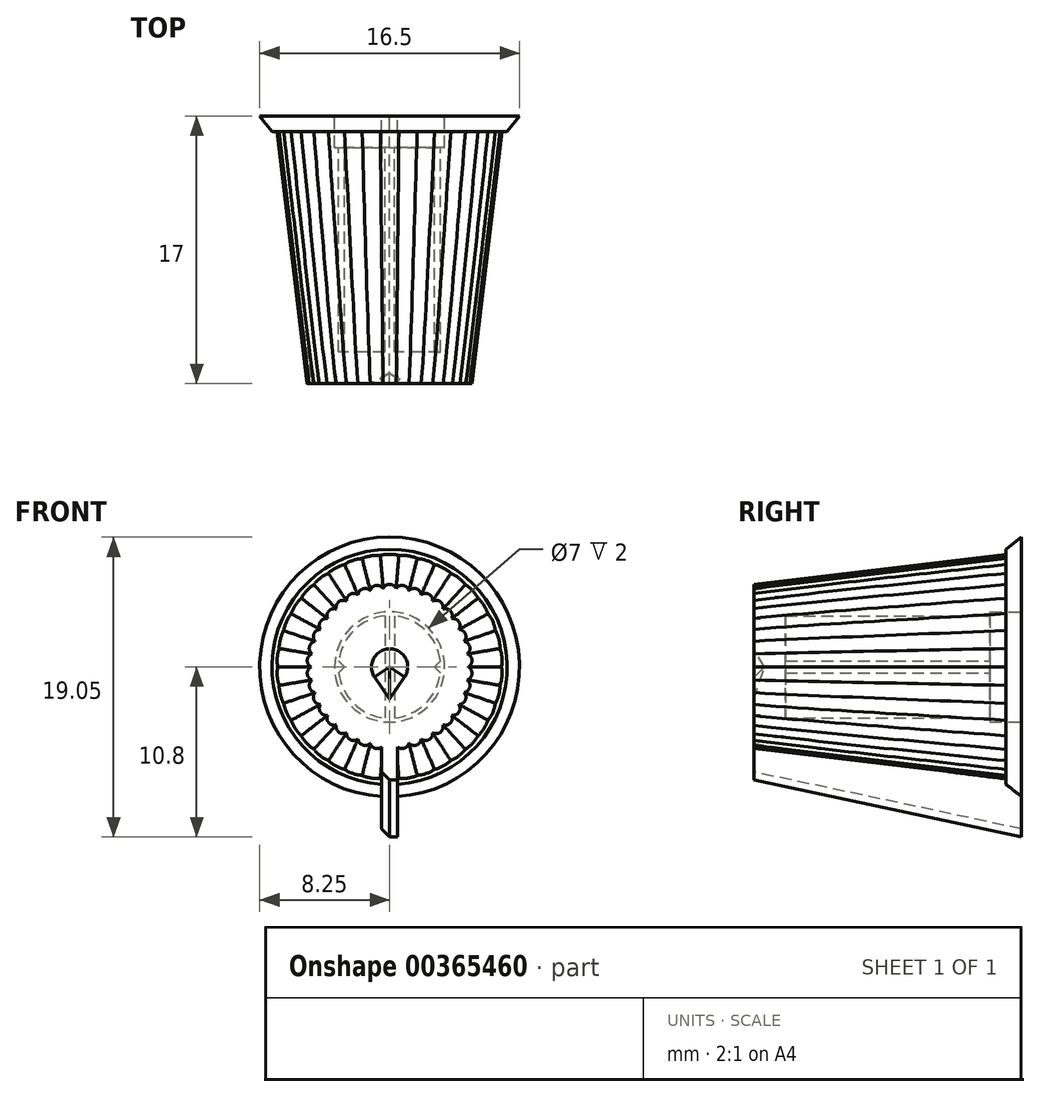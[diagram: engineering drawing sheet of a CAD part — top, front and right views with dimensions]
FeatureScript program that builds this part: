
annotation { "Feature Type Name" : "Feature", "Feature Type Description" : "" }
export const myFeature = defineFeature(function(context is Context, id is Id, definition is map)
    precondition{}
    {
        {
            var Q0;
            Q0=qCreatedBy(makeId("Front.planeOp"),FACE);
            var sketch = newSketch(context, id + "F0", { "sketchPlane" : qUnion([Q0])});
            skCircle(sketch, "E0", {"center": v(0, 0) * mm, "radius": 8.25 * mm});
            skSolve(sketch);
        }
        {
            var Q0;
            Q0 = qSketchRegion(id + "F0", true);
            extrude(context, id + "F1", {"entities" : qUnion([Q0]), "depth" : 1 * mm, "hasDraft" : true, "draftAngle" : 38 * degree, "draftPullDirection" : true});
        }
        {
            var Q0;
            Q0=qCreatedBy(makeId("Front.planeOp"),FACE);
            cPlane(context, id + "F2", {"entities" : qUnion([Q0]), "cplaneType" : CPlaneType.OFFSET, "offset" : 17 * mm, "width" : 150 * mm, "height" : 150 * mm});
        }
        {
            var Q0;
            Q0=qCreatedBy(id+"F2.planeOp",FACE);
            var sketch = newSketch(context, id + "F3", { "sketchPlane" : qUnion([Q0])});
            skArc(sketch, "E1", {"start": v(0.41, 4.98) * mm, "mid": v(0, 5.25) * mm, "end": v(-0.41, 4.98) * mm});
            skArc(sketch, "E2.1.0", {"start": v(-0.41, 4.98) * mm, "mid": v(-0.86, 5.18) * mm, "end": v(-1.23, 4.84) * mm});
            skArc(sketch, "E2.2.0", {"start": v(-1.23, 4.84) * mm, "mid": v(-1.7, 4.97) * mm, "end": v(-2, 4.58) * mm});
            skArc(sketch, "E2.3.0", {"start": v(-2, 4.58) * mm, "mid": v(-2.5, 4.62) * mm, "end": v(-2.73, 4.18) * mm});
            skArc(sketch, "E2.4.0", {"start": v(-2.73, 4.18) * mm, "mid": v(-3.22, 4.14) * mm, "end": v(-3.38, 3.68) * mm});
            skArc(sketch, "E2.5.0", {"start": v(-3.38, 3.68) * mm, "mid": v(-3.86, 3.56) * mm, "end": v(-3.94, 3.07) * mm});
            skArc(sketch, "E2.6.0", {"start": v(-3.94, 3.07) * mm, "mid": v(-4.4, 2.87) * mm, "end": v(-4.4, 2.38) * mm});
            skArc(sketch, "E2.7.0", {"start": v(-4.4, 2.38) * mm, "mid": v(-4.8, 2.1) * mm, "end": v(-4.73, 1.62) * mm});
            skArc(sketch, "E2.8.0", {"start": v(-4.73, 1.62) * mm, "mid": v(-5.09, 1.29) * mm, "end": v(-4.93, 0.82) * mm});
            skArc(sketch, "E2.9.0", {"start": v(-4.93, 0.82) * mm, "mid": v(-5.23, 0.43) * mm, "end": v(-5, 0) * mm});
            skArc(sketch, "E2.10.0", {"start": v(-5, 0) * mm, "mid": v(-5.23, -0.43) * mm, "end": v(-4.93, -0.82) * mm});
            skArc(sketch, "E2.11.0", {"start": v(-4.93, -0.82) * mm, "mid": v(-5.09, -1.29) * mm, "end": v(-4.73, -1.62) * mm});
            skArc(sketch, "E2.12.0", {"start": v(-4.73, -1.62) * mm, "mid": v(-4.8, -2.1) * mm, "end": v(-4.4, -2.38) * mm});
            skArc(sketch, "E2.13.0", {"start": v(-4.4, -2.38) * mm, "mid": v(-4.4, -2.87) * mm, "end": v(-3.94, -3.07) * mm});
            skArc(sketch, "E2.14.0", {"start": v(-3.94, -3.07) * mm, "mid": v(-3.86, -3.56) * mm, "end": v(-3.38, -3.68) * mm});
            skArc(sketch, "E2.15.0", {"start": v(-3.38, -3.68) * mm, "mid": v(-3.22, -4.14) * mm, "end": v(-2.73, -4.18) * mm});
            skArc(sketch, "E2.16.0", {"start": v(-2.73, -4.18) * mm, "mid": v(-2.5, -4.62) * mm, "end": v(-2, -4.58) * mm});
            skArc(sketch, "E2.17.0", {"start": v(-2, -4.58) * mm, "mid": v(-1.7, -4.97) * mm, "end": v(-1.23, -4.84) * mm});
            skArc(sketch, "E2.18.0", {"start": v(-1.23, -4.84) * mm, "mid": v(-0.86, -5.18) * mm, "end": v(-0.41, -4.98) * mm});
            skArc(sketch, "E2.19.0", {"start": v(-0.41, -4.98) * mm, "mid": v(0, -5.25) * mm, "end": v(0.41, -4.98) * mm});
            skArc(sketch, "E2.20.0", {"start": v(0.41, -4.98) * mm, "mid": v(0.86, -5.18) * mm, "end": v(1.23, -4.84) * mm});
            skArc(sketch, "E2.21.0", {"start": v(1.23, -4.84) * mm, "mid": v(1.7, -4.97) * mm, "end": v(2, -4.58) * mm});
            skArc(sketch, "E2.22.0", {"start": v(2, -4.58) * mm, "mid": v(2.5, -4.62) * mm, "end": v(2.73, -4.18) * mm});
            skArc(sketch, "E2.23.0", {"start": v(2.73, -4.18) * mm, "mid": v(3.22, -4.14) * mm, "end": v(3.38, -3.68) * mm});
            skArc(sketch, "E2.24.0", {"start": v(3.38, -3.68) * mm, "mid": v(3.86, -3.56) * mm, "end": v(3.94, -3.07) * mm});
            skArc(sketch, "E2.25.0", {"start": v(3.94, -3.07) * mm, "mid": v(4.4, -2.87) * mm, "end": v(4.4, -2.38) * mm});
            skArc(sketch, "E2.26.0", {"start": v(4.4, -2.38) * mm, "mid": v(4.8, -2.1) * mm, "end": v(4.73, -1.62) * mm});
            skArc(sketch, "E2.27.0", {"start": v(4.73, -1.62) * mm, "mid": v(5.09, -1.29) * mm, "end": v(4.93, -0.82) * mm});
            skArc(sketch, "E2.28.0", {"start": v(4.93, -0.82) * mm, "mid": v(5.23, -0.43) * mm, "end": v(5, 0) * mm});
            skArc(sketch, "E2.29.0", {"start": v(5, 0) * mm, "mid": v(5.23, 0.43) * mm, "end": v(4.93, 0.82) * mm});
            skArc(sketch, "E2.30.0", {"start": v(4.93, 0.82) * mm, "mid": v(5.09, 1.29) * mm, "end": v(4.73, 1.62) * mm});
            skArc(sketch, "E2.31.0", {"start": v(4.73, 1.62) * mm, "mid": v(4.8, 2.1) * mm, "end": v(4.4, 2.38) * mm});
            skArc(sketch, "E2.32.0", {"start": v(4.4, 2.38) * mm, "mid": v(4.4, 2.87) * mm, "end": v(3.94, 3.07) * mm});
            skArc(sketch, "E2.33.0", {"start": v(3.94, 3.07) * mm, "mid": v(3.86, 3.56) * mm, "end": v(3.38, 3.68) * mm});
            skArc(sketch, "E2.34.0", {"start": v(3.38, 3.68) * mm, "mid": v(3.22, 4.14) * mm, "end": v(2.73, 4.18) * mm});
            skArc(sketch, "E2.35.0", {"start": v(2.73, 4.18) * mm, "mid": v(2.5, 4.62) * mm, "end": v(2, 4.58) * mm});
            skArc(sketch, "E2.36.0", {"start": v(2, 4.58) * mm, "mid": v(1.7, 4.97) * mm, "end": v(1.23, 4.84) * mm});
            skArc(sketch, "E2.37.0", {"start": v(1.23, 4.84) * mm, "mid": v(0.86, 5.18) * mm, "end": v(0.41, 4.98) * mm});
            skPoint(sketch, "E2.center", {"position": v(0, 0) * mm});
            skSolve(sketch);
        }
        {
            var Q0;
            Q0 = qSketchRegion(id + "F3", true);
            extrude(context, id + "F4", {"entities" : qUnion([Q0]), "operationType" : NewBodyOperationType.ADD, "oppositeDirection" : true, "depth" : 16 * mm, "hasDraft" : true, "draftAngle" : 6.8 * degree});
        }
        {
            var Q0;
            Q0=qCreatedBy(makeId("Right.planeOp"),FACE);
            var sketch = newSketch(context, id + "F5", { "sketchPlane" : qUnion([Q0])});
            skLineSegment(sketch, "E3", {"start": v(0, 0) * mm, "end": v(0, -10.8) * mm});
            skLineSegment(sketch, "E4", {"start": v(0, -10.8) * mm, "end": v(-17, -7.19) * mm});
            skLineSegment(sketch, "E5", {"start": v(0, 0) * mm, "end": v(-17, 0) * mm});
            skLineSegment(sketch, "E6", {"start": v(-17, 0) * mm, "end": v(-17, -7.19) * mm});
            skSolve(sketch);
        }
        {
            var Q0;
            Q0 = qSketchRegion(id + "F5", true);
            extrude(context, id + "F6", {"entities" : qUnion([Q0]), "operationType" : NewBodyOperationType.ADD, "endBound" : BoundingType.SYMMETRIC, "oppositeDirection" : true, "depth" : 1 * mm});
        }
        {
            var Q0;
            Q0=makeQuery(id+"F6.opExtrude","CAP_EDGE",EDGE,{"disambiguationData":[OSD([sQuery(id+"F5.wireOp",EDGE,"E4")])],"isStart":false});
            chamfer(context, id + "F7", {"entities" : qUnion([Q0]), "width" : 0.5 * mm, "tangentPropagation" : true});
        }
        {
            var Q0;
            Q0=makeQuery(id+"F6.boolean.opBoolean","MERGE",FACE,{"derivedFrom":[makeQuery(id+"F1.opExtrude","CAP_FACE",FACE,{"disambiguationData":[OSD([sQuery(id+"F0.wireOp",EDGE,"E0")])],"isStart":true}),makeQuery(id+"F6.opExtrude","SWEPT_FACE",FACE,{"disambiguationData":[OSD([sQuery(id+"F5.wireOp",EDGE,"E3")])]})]});
            var sketch = newSketch(context, id + "F8", { "sketchPlane" : qUnion([Q0])});
            skArc(sketch, "E7", {"start": v(0.3, -3.24) * mm, "mid": v(2.27, -2.33) * mm, "end": v(3.23, -0.38) * mm});
            skLineSegment(sketch, "E8.left", {"start": v(0.3, -3.24) * mm, "end": v(0.3, 3.24) * mm});
            skLineSegment(sketch, "E8.right", {"start": v(-0.3, -3.24) * mm, "end": v(-0.3, 3.24) * mm});
            skPoint(sketch, "E8.top.end.orphan", {"position": v(-0.3, 5.12) * mm});
            skPoint(sketch, "E8.top.start.orphan", {"position": v(0.3, 5.12) * mm});
            skPoint(sketch, "E9.orphan", {"position": v(0.3, -5.12) * mm});
            skPoint(sketch, "E10.orphan", {"position": v(-0.3, -5.12) * mm});
            skArc(sketch, "E11.trimOffspring", {"start": v(-0.3, 3.24) * mm, "mid": v(-2.27, 2.33) * mm, "end": v(-3.23, 0.38) * mm});
            skPoint(sketch, "E12.endSnap0", {"position": v(3.25, 0) * mm});
            skLineSegment(sketch, "E13", {"start": v(2.85, 0) * mm, "end": v(3.23, -0.38) * mm});
            skLineSegment(sketch, "E14.MirrorCS", {"start": v(2.85, 0) * mm, "end": v(3.23, 0.38) * mm});
            skLineSegment(sketch, "E15.MirrorCS", {"start": v(-2.85, 0) * mm, "end": v(-3.23, 0.38) * mm});
            skLineSegment(sketch, "E16.MirrorCS", {"start": v(-2.85, 0) * mm, "end": v(-3.23, -0.38) * mm});
            skArc(sketch, "E17.trimOffspring", {"start": v(-3.23, -0.38) * mm, "mid": v(-2.27, -2.33) * mm, "end": v(-0.3, -3.24) * mm});
            skPoint(sketch, "E18.orphan", {"position": v(-3.25, 0.4) * mm});
            skPoint(sketch, "E19.orphan", {"position": v(-3.25, -0.4) * mm});
            skPoint(sketch, "E20.orphan", {"position": v(3.25, 0.4) * mm});
            skArc(sketch, "E21.trimOffspring", {"start": v(3.23, 0.38) * mm, "mid": v(2.27, 2.33) * mm, "end": v(0.3, 3.24) * mm});
            skPoint(sketch, "E22.orphan", {"position": v(3.25, -0.4) * mm});
            skSolve(sketch);
        }
        {
            var Q0;
            Q0 = qSketchRegion(id + "F8", true);
            extrude(context, id + "F9", {"entities" : qUnion([Q0]), "operationType" : NewBodyOperationType.REMOVE, "oppositeDirection" : true, "depth" : 15 * mm});
        }
        {
            var Q0;
            Q0=makeQuery(id+"F6.boolean.opBoolean","MERGE",FACE,{"derivedFrom":[makeQuery(id+"F1.opExtrude","CAP_FACE",FACE,{"disambiguationData":[OSD([sQuery(id+"F0.wireOp",EDGE,"E0")])],"isStart":true}),makeQuery(id+"F6.opExtrude","SWEPT_FACE",FACE,{"disambiguationData":[OSD([sQuery(id+"F5.wireOp",EDGE,"E3")])]})]});
            var sketch = newSketch(context, id + "F10", { "sketchPlane" : qUnion([Q0])});
            skCircle(sketch, "E23", {"center": v(0, 0) * mm, "radius": 3.5 * mm});
            skSolve(sketch);
        }
        {
            var Q0;
            Q0 = qSketchRegion(id + "F10", true);
            extrude(context, id + "F11", {"entities" : qUnion([Q0]), "operationType" : NewBodyOperationType.REMOVE, "oppositeDirection" : true, "depth" : 2 * mm});
        }
        {
            var Q0;
            Q0=makeQuery(id+"F6.boolean.opBoolean","MERGE",FACE,{"derivedFrom":[makeQuery(id+"F4.opExtrude","CAP_FACE",FACE,{"disambiguationData":[OSD([sQuery(id+"F3.wireOp",EDGE,"E1"),sQuery(id+"F3.wireOp",EDGE,"E2.1.0"),sQuery(id+"F3.wireOp",EDGE,"E2.2.0"),sQuery(id+"F3.wireOp",EDGE,"E2.3.0"),sQuery(id+"F3.wireOp",EDGE,"E2.4.0"),sQuery(id+"F3.wireOp",EDGE,"E2.5.0"),sQuery(id+"F3.wireOp",EDGE,"E2.6.0"),sQuery(id+"F3.wireOp",EDGE,"E2.7.0"),sQuery(id+"F3.wireOp",EDGE,"E2.8.0"),sQuery(id+"F3.wireOp",EDGE,"E2.9.0"),sQuery(id+"F3.wireOp",EDGE,"E2.10.0"),sQuery(id+"F3.wireOp",EDGE,"E2.11.0"),sQuery(id+"F3.wireOp",EDGE,"E2.12.0"),sQuery(id+"F3.wireOp",EDGE,"E2.13.0"),sQuery(id+"F3.wireOp",EDGE,"E2.14.0"),sQuery(id+"F3.wireOp",EDGE,"E2.15.0"),sQuery(id+"F3.wireOp",EDGE,"E2.16.0"),sQuery(id+"F3.wireOp",EDGE,"E2.17.0"),sQuery(id+"F3.wireOp",EDGE,"E2.18.0"),sQuery(id+"F3.wireOp",EDGE,"E2.19.0"),sQuery(id+"F3.wireOp",EDGE,"E2.20.0"),sQuery(id+"F3.wireOp",EDGE,"E2.21.0"),sQuery(id+"F3.wireOp",EDGE,"E2.22.0"),sQuery(id+"F3.wireOp",EDGE,"E2.23.0"),sQuery(id+"F3.wireOp",EDGE,"E2.24.0"),sQuery(id+"F3.wireOp",EDGE,"E2.25.0"),sQuery(id+"F3.wireOp",EDGE,"E2.26.0"),sQuery(id+"F3.wireOp",EDGE,"E2.27.0"),sQuery(id+"F3.wireOp",EDGE,"E2.28.0"),sQuery(id+"F3.wireOp",EDGE,"E2.29.0"),sQuery(id+"F3.wireOp",EDGE,"E2.30.0"),sQuery(id+"F3.wireOp",EDGE,"E2.31.0"),sQuery(id+"F3.wireOp",EDGE,"E2.32.0"),sQuery(id+"F3.wireOp",EDGE,"E2.33.0"),sQuery(id+"F3.wireOp",EDGE,"E2.34.0"),sQuery(id+"F3.wireOp",EDGE,"E2.35.0"),sQuery(id+"F3.wireOp",EDGE,"E2.36.0"),sQuery(id+"F3.wireOp",EDGE,"E2.37.0")])],"isStart":true}),makeQuery(id+"F6.opExtrude","SWEPT_FACE",FACE,{"disambiguationData":[OSD([sQuery(id+"F5.wireOp",EDGE,"E6")])]})]});
            var sketch = newSketch(context, id + "F12", { "sketchPlane" : qUnion([Q0])});
            skArc(sketch, "E24", {"start": v(0.95, -0.65) * mm, "mid": v(0, 1.15) * mm, "end": v(-0.95, -0.65) * mm});
            skLineSegment(sketch, "E25", {"start": v(0, -2.04) * mm, "end": v(-0.95, -0.65) * mm});
            skLineSegment(sketch, "E26.MirrorCS", {"start": v(0, -2.04) * mm, "end": v(0.95, -0.65) * mm});
            skSolve(sketch);
        }
        {
            var Q0;
            Q0 = qSketchRegion(id + "F12", true);
            extrude(context, id + "F13", {"entities" : qUnion([Q0]), "operationType" : NewBodyOperationType.REMOVE, "oppositeDirection" : true, "depth" : 0.8 * mm, "hasDraft" : true, "draftAngle" : 60 * degree, "draftPullDirection" : true});
        }
    });
